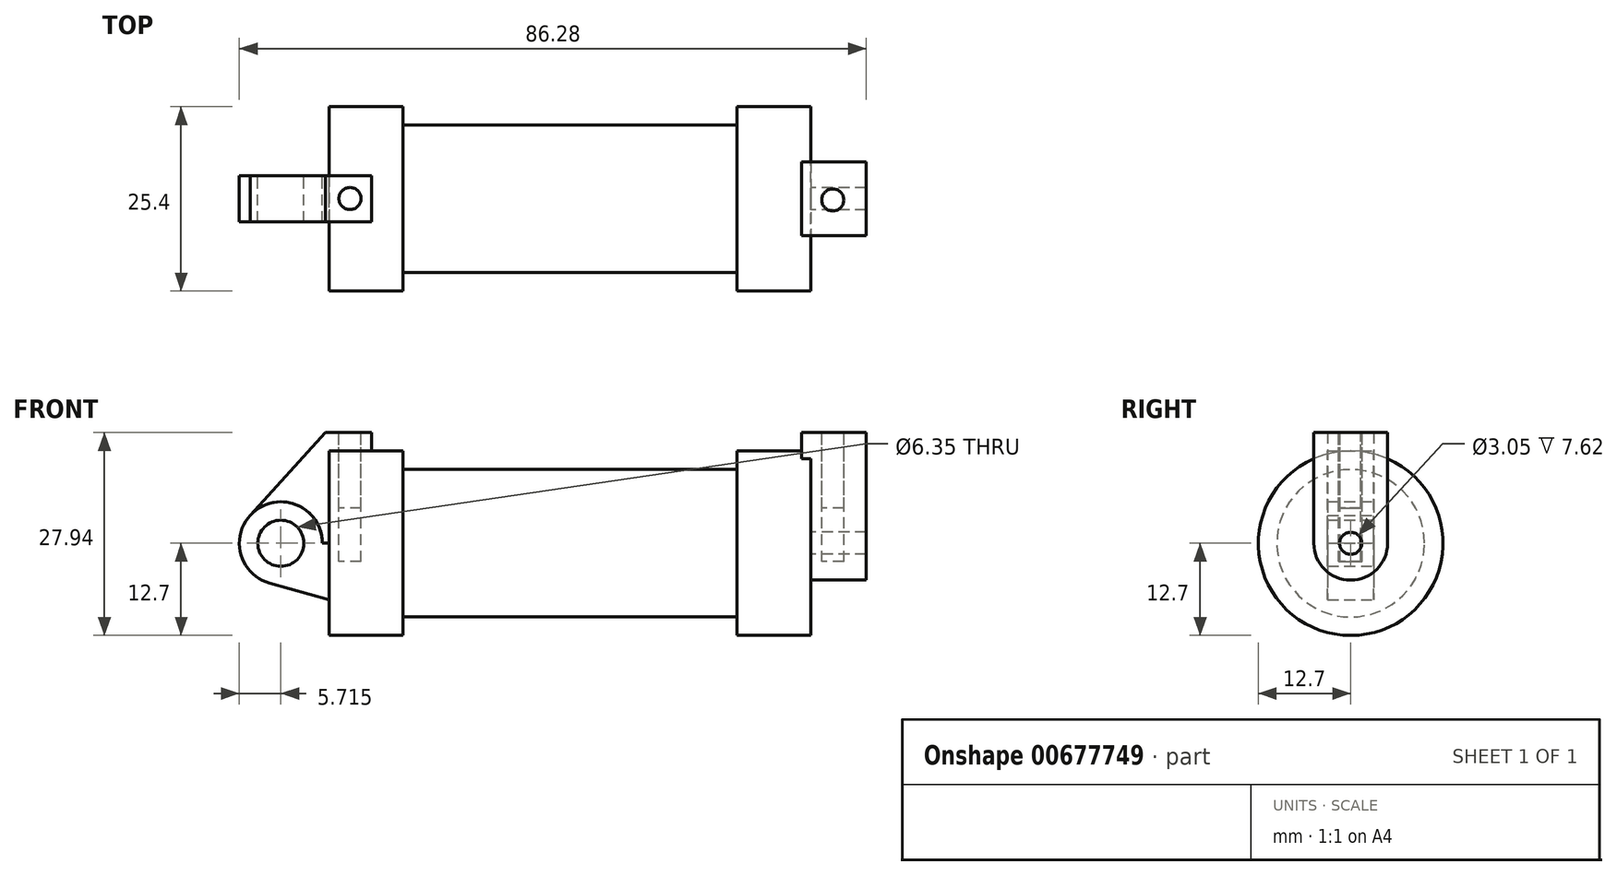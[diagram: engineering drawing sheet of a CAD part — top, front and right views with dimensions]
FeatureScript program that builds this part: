
annotation { "Feature Type Name" : "Feature", "Feature Type Description" : "" }
export const myFeature = defineFeature(function(context is Context, id is Id, definition is map)
    precondition{}
    {
        {
            var Q0;
            Q0=qCreatedBy(makeId("Front.planeOp"),FACE);
            var sketch = newSketch(context, id + "F0", { "sketchPlane" : qUnion([Q0])});
            skLineSegment(sketch, "E0", {"start": v(0, 0) * mm, "end": v(0, 12.7) * mm});
            skLineSegment(sketch, "E1", {"start": v(0, 12.7) * mm, "end": v(10.16, 12.7) * mm});
            skLineSegment(sketch, "E2", {"start": v(10.16, 12.7) * mm, "end": v(10.16, 10.16) * mm});
            skLineSegment(sketch, "E3", {"start": v(10.16, 10.16) * mm, "end": v(56.13, 10.16) * mm});
            skLineSegment(sketch, "E4", {"start": v(56.13, 10.16) * mm, "end": v(56.13, 12.7) * mm});
            skLineSegment(sketch, "E5", {"start": v(56.13, 12.7) * mm, "end": v(66.3, 12.7) * mm});
            skLineSegment(sketch, "E6", {"start": v(66.3, 12.7) * mm, "end": v(66.3, 0) * mm});
            skLineSegment(sketch, "E7", {"start": v(66.3, 0) * mm, "end": v(0, 0) * mm});
            skLineSegment(sketch, "E8", {"start": v(5.84, 15.24) * mm, "end": v(-0.5, 15.24) * mm});
            skLineSegment(sketch, "E9", {"start": v(-0.5, 15.24) * mm, "end": v(-10.88, 3.85) * mm});
            skLineSegment(sketch, "E10", {"start": v(0, 0) * mm, "end": v(-6.65, 0) * mm});
            skCircle(sketch, "E11", {"center": v(-6.65, 0) * mm, "radius": 5.72 * mm});
            skCircle(sketch, "E12", {"center": v(-6.65, 0) * mm, "radius": 3.18 * mm});
            skLineSegment(sketch, "E13", {"start": v(5.84, 15.24) * mm, "end": v(5.84, -9.4) * mm});
            skLineSegment(sketch, "E14", {"start": v(5.84, -9.4) * mm, "end": v(-8.18, -5.5) * mm});
            skSolve(sketch);
        }
        {
            var Q0;
            {var subQ0=sQuery(id+"F0.wireOp",EDGE,"E2");Q0=makeQuery(id+"F0.imprint","IMPRINT",FACE,{"disambiguationData":[TD([[makeQuery(id+"F0.imprint","IMPRINT",EDGE,{"derivedFrom":subQ0}),-1.0]])]});}
            var Q1;
            {var subQ0=sQuery(id+"F0.wireOp",EDGE,"E0");Q1=makeQuery(id+"F0.imprint","IMPRINT",FACE,{"disambiguationData":[TD([[makeQuery(id+"F0.imprint","IMPRINT",EDGE,{"derivedFrom":subQ0}),-1.0]])]});}
            var Q2;
            Q2=sQuery(id+"F0.wireOp",EDGE,"E7");
            revolve(context, id + "F1", {"entities" : qUnion([Q0, Q1]), "axis" : qUnion([Q2]), "revolveType" : RevolveType.FULL});
        }
        {
            var Q0;
            {var subQ5=sQuery(id+"F0.wireOp",EDGE,"E12");Q0=makeQuery(id+"F0.imprint","IMPRINT",FACE,{"disambiguationData":[TD([[makeQuery(id+"F0.imprint","IMPRINT",EDGE,{"derivedFrom":subQ5}),-1.0]])]});}
            var Q1;
            {var subQ0=sQuery(id+"F0.wireOp",EDGE,"E14");Q1=makeQuery(id+"F0.imprint","IMPRINT",FACE,{"disambiguationData":[TD([[makeQuery(id+"F0.imprint","IMPRINT",EDGE,{"derivedFrom":subQ0}),-1.0]])]});}
            extrude(context, id + "F2", {"entities" : qUnion([Q0, Q1]), "operationType" : NewBodyOperationType.ADD, "endBound" : BoundingType.SYMMETRIC, "depth" : 6.35 * mm, "offsetDistance" : 25.4 * mm, "hasSecondDirection" : true, "secondDirectionOppositeDirection" : true, "secondDirectionDepth" : 25.4 * mm});
        }
        {
            var Q0;
            {var subQ1=sQuery(id+"F0.wireOp",EDGE,"E0");Q0=makeQuery(id+"F0.imprint","IMPRINT",FACE,{"disambiguationData":[TD([[makeQuery(id+"F0.imprint","IMPRINT",EDGE,{"derivedFrom":subQ1}),1.0]])]});}
            extrude(context, id + "F3", {"entities" : qUnion([Q0]), "endBound" : BoundingType.SYMMETRIC, "depth" : 6.35 * mm, "offsetDistance" : 25.4 * mm});
        }
        {
            var Q0;
            Q0=makeQuery(id+"F1.opRevolve","SWEPT_FACE",FACE,{"disambiguationData":[OSD([sQuery(id+"F0.wireOp",EDGE,"E6")])]});
            var sketch = newSketch(context, id + "F4", { "sketchPlane" : qUnion([Q0])});
            skCircle(sketch, "E15", {"center": v(0, 0) * mm, "radius": 1.52 * mm});
            skCircle(sketch, "E16", {"center": v(0, 0) * mm, "radius": 5.08 * mm});
            skLineSegment(sketch, "E17", {"start": v(-5.08, 0) * mm, "end": v(-5.08, 15.24) * mm});
            skLineSegment(sketch, "E18", {"start": v(5.08, 0) * mm, "end": v(5.08, 15.24) * mm});
            skLineSegment(sketch, "E19", {"start": v(5.08, 15.24) * mm, "end": v(-5.08, 15.24) * mm});
            skSolve(sketch);
        }
        {
            var Q0;
            Q0 = qSketchRegion(id + "F4", true);
            extrude(context, id + "F5", {"entities" : qUnion([Q0]), "operationType" : NewBodyOperationType.ADD, "depth" : 7.62 * mm, "offsetDistance" : 25.4 * mm, "hasSecondDirection" : true, "secondDirectionOppositeDirection" : true, "secondDirectionDepth" : 1.27 * mm});
        }
        {
            var Q0;
            Q0=makeQuery(id+"F5.opExtrude","SWEPT_FACE",FACE,{"disambiguationData":[OSD([sQuery(id+"F4.wireOp",EDGE,"E19")])]});
            var sketch = newSketch(context, id + "F6", { "sketchPlane" : qUnion([Q0])});
            skSolve(sketch);
        }
        {
            var Q0;
            {var subQ0=sQuery(id+"F4.wireOp",EDGE,"E19");Q0=makeQuery(id+"F6.imprint","IMPRINT",FACE,{"disambiguationData":[TD([[makeQuery(id+"F6.imprint","IMPRINT",EDGE,{"derivedFrom":makeQuery(id+"F5.opExtrude","CAP_EDGE",EDGE,{"disambiguationData":[OSD([subQ0])],"isStart":true})}),1.0]])]});}
            var sketch = newSketch(context, id + "F7", { "sketchPlane" : qUnion([Q0])});
            skCircle(sketch, "E20", {"center": v(69.3, -0.14) * mm, "radius": 1.52 * mm});
            skCircle(sketch, "E21", {"center": v(2.86, 0.06) * mm, "radius": 1.52 * mm});
            skSolve(sketch);
        }
        {
            var Q0;
            Q0=makeQuery(id+"F7.imprint","IMPRINT",FACE,{"disambiguationData":[TD([[makeQuery(id+"F7.imprint","IMPRINT",EDGE,{"derivedFrom":sQuery(id+"F7.wireOp",EDGE,"E20")}),1.0]])]});
            var Q1;
            Q1=makeQuery(id+"F7.imprint","IMPRINT",FACE,{"disambiguationData":[TD([[makeQuery(id+"F7.imprint","IMPRINT",EDGE,{"derivedFrom":sQuery(id+"F7.wireOp",EDGE,"E21")}),1.0]])]});
            extrude(context, id + "F8", {"entities" : qUnion([Q0, Q1]), "oppositeDirection" : true, "depth" : 17.78 * mm, "offsetDistance" : 25.4 * mm});
        }
        {
            var Q0;
            Q0=makeQuery(id+"F8.opExtrude","CAP_FACE",FACE,{"disambiguationData":[OSD([sQuery(id+"F7.wireOp",EDGE,"E21")])],"isStart":true});
            extrude(context, id + "F9", {"entities" : qUnion([Q0]), "oppositeDirection" : true, "depth" : 17.78 * mm, "offsetDistance" : 25.4 * mm});
        }
        {
            var Q0;
            Q0 = qSketchRegion(id + "F7", true);
            extrude(context, id + "F10", {"entities" : qUnion([Q0]), "oppositeDirection" : true, "depth" : 10.4 * mm, "offsetDistance" : 25.4 * mm});
        }
    });
